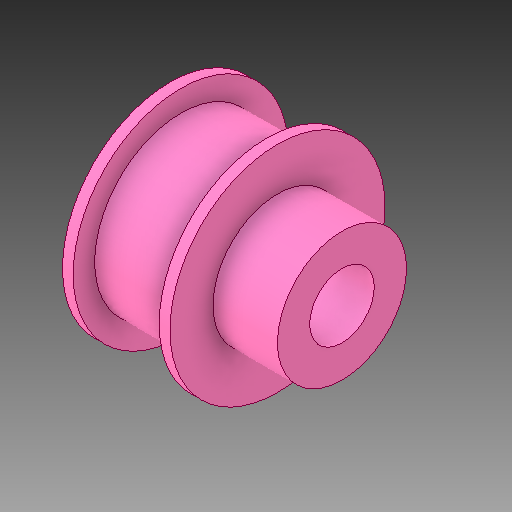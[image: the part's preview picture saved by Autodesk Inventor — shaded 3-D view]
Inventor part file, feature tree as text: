
AUTODESK INVENTOR PART (.ipt)
format: ipt  version: 2017 SP1 (Build 210196100, 196)  size: 162,304 bytes
history: native  units: in
note: dims shown in document units (in); Inventor stores cm internally (conversion verified against a paired STEP export)
features: extrude x4, sketch x4
ambient origin geometry x8: Origin, YZ Plane, XZ Plane, XY Plane, X Axis, Y Axis, Z Axis, Center Point
bodies: Solid1 (feature_tree)
feature tree (8):
  extrude  "Extrusion1"  Depth=0.375in
  extrude  "Extrusion2"  Depth=0.5in
  extrude  "Extrusion3"  Depth=0.0625in TaperAngle=0.0deg
  extrude  "Extrusion4"  Depth=0.375in TaperAngle=0.0deg
  sketch  "Sketch1"  dims[d0=1.0in d2=0.375in]
  sketch  "Sketch2"  dims[d4=0.5in d5=0.0in d6=0.125in]
  sketch  "Sketch3"  dims[d7=0.0625in d8=0.0in d9=0.0625in d10=0.0in]
  sketch  "Sketch4"  dims[d11=0.1875in d12=0.375in d13=0.0in]
